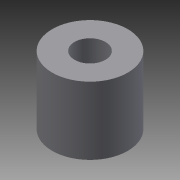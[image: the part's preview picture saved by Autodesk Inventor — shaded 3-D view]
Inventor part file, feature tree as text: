
AUTODESK INVENTOR PART (.ipt)
format: ipt  version: 2013 (Build 170138000, 138)  size: 72,192 bytes
history: native  units: mm
features: extrude x1, sketch x1
ambient origin geometry x8: Origin, YZ Plane, XZ Plane, XY Plane, X Axis, Y Axis, Z Axis, Center Point
bodies: Solid1 (feature_tree)
feature tree (2):
  extrude  "Extrusion1"  Depth=3.2mm
  sketch  "Sketch1"  dims[d0=7.8mm d2=3.2mm d3=7.0mm d4=0.0mm]
